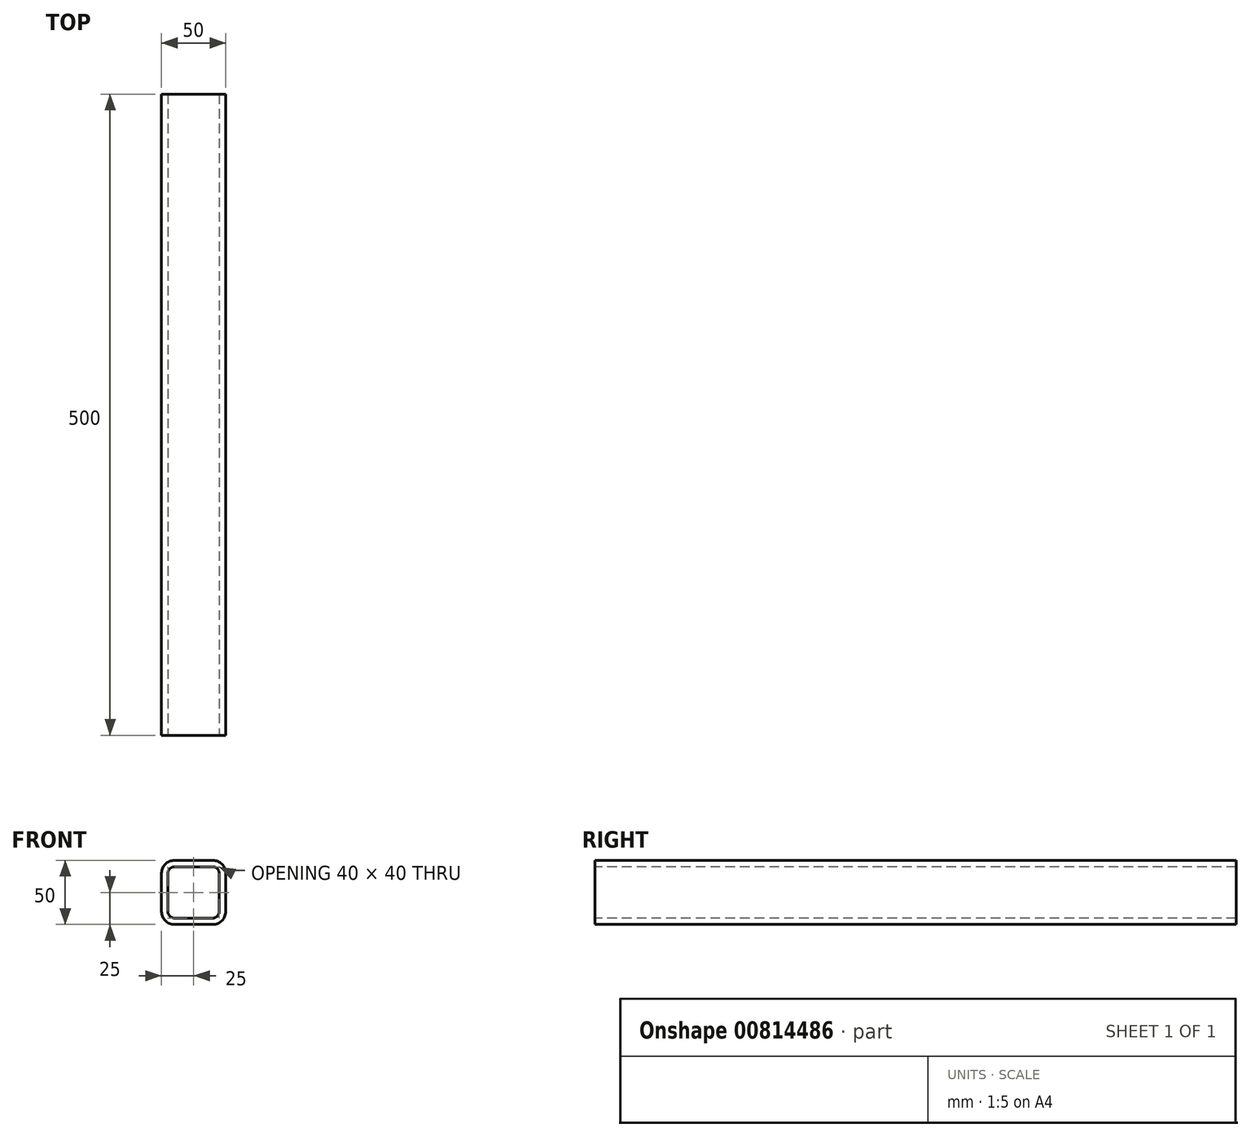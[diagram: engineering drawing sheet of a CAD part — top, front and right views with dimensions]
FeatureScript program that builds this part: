
annotation { "Feature Type Name" : "Feature", "Feature Type Description" : "" }
export const myFeature = defineFeature(function(context is Context, id is Id, definition is map)
    precondition{}
    {
        {
            var Q0;
            Q0=qCreatedBy(makeId("Front.planeOp"),FACE);
            var sketch = newSketch(context, id + "F0", { "sketchPlane" : qUnion([Q0])});
            skLineSegment(sketch, "E0.bottom", {"start": v(15, -25) * mm, "end": v(-15, -25) * mm});
            skLineSegment(sketch, "E0.top", {"start": v(15, 25) * mm, "end": v(-15, 25) * mm});
            skLineSegment(sketch, "E0.left", {"start": v(25, -15) * mm, "end": v(25, 15) * mm});
            skLineSegment(sketch, "E0.right", {"start": v(-25, -15) * mm, "end": v(-25, 15) * mm});
            skPoint(sketch, "E0.middle", {"position": v(0, 0) * mm});
            skPoint(sketch, "E1.visualSharp", {"position": v(-25, 25) * mm});
            skArc(sketch, "E1.filletArc", {"start": v(-15, 25) * mm, "mid": v(-22.07, 22.07) * mm, "end": v(-25, 15) * mm});
            skPoint(sketch, "E2.visualSharp", {"position": v(25, 25) * mm});
            skArc(sketch, "E2.filletArc", {"start": v(25, 15) * mm, "mid": v(22.07, 22.07) * mm, "end": v(15, 25) * mm});
            skPoint(sketch, "E3.visualSharp", {"position": v(25, -25) * mm});
            skArc(sketch, "E3.filletArc", {"start": v(15, -25) * mm, "mid": v(22.07, -22.07) * mm, "end": v(25, -15) * mm});
            skPoint(sketch, "E4.visualSharp", {"position": v(-25, -25) * mm});
            skArc(sketch, "E4.filletArc", {"start": v(-25, -15) * mm, "mid": v(-22.07, -22.07) * mm, "end": v(-15, -25) * mm});
            skArc(sketch, "E5.0", {"start": v(15, -20) * mm, "mid": v(18.54, -18.54) * mm, "end": v(20, -15) * mm});
            skLineSegment(sketch, "E5.1", {"start": v(15, -20) * mm, "end": v(-15, -20) * mm});
            skLineSegment(sketch, "E5.2", {"start": v(20, -15) * mm, "end": v(20, 15) * mm});
            skArc(sketch, "E5.3", {"start": v(-20, -15) * mm, "mid": v(-18.54, -18.54) * mm, "end": v(-15, -20) * mm});
            skArc(sketch, "E5.4", {"start": v(20, 15) * mm, "mid": v(18.54, 18.54) * mm, "end": v(15, 20) * mm});
            skLineSegment(sketch, "E5.5", {"start": v(15, 20) * mm, "end": v(-15, 20) * mm});
            skArc(sketch, "E5.6", {"start": v(-15, 20) * mm, "mid": v(-18.54, 18.54) * mm, "end": v(-20, 15) * mm});
            skLineSegment(sketch, "E5.7", {"start": v(-20, -15) * mm, "end": v(-20, 15) * mm});
            skSolve(sketch);
        }
        {
            assignVariable(context, id + "F1", {"name" : "Length", "anyValue" : 500});
        }
        {
            var Q0;
            Q0=makeQuery(id+"F0.imprint","IMPRINT",FACE,{"disambiguationData":[TD([[makeQuery(id+"F0.imprint","IMPRINT",EDGE,{"derivedFrom":sQuery(id+"F0.wireOp",EDGE,"E0.bottom")}),-1.0]])]});
            extrude(context, id + "F2", {"entities" : qUnion([Q0]), "oppositeDirection" : true, "depth" : (getVariable(context, 'Length')) * mm, "offsetDistance" : 25 * mm});
        }
    });
